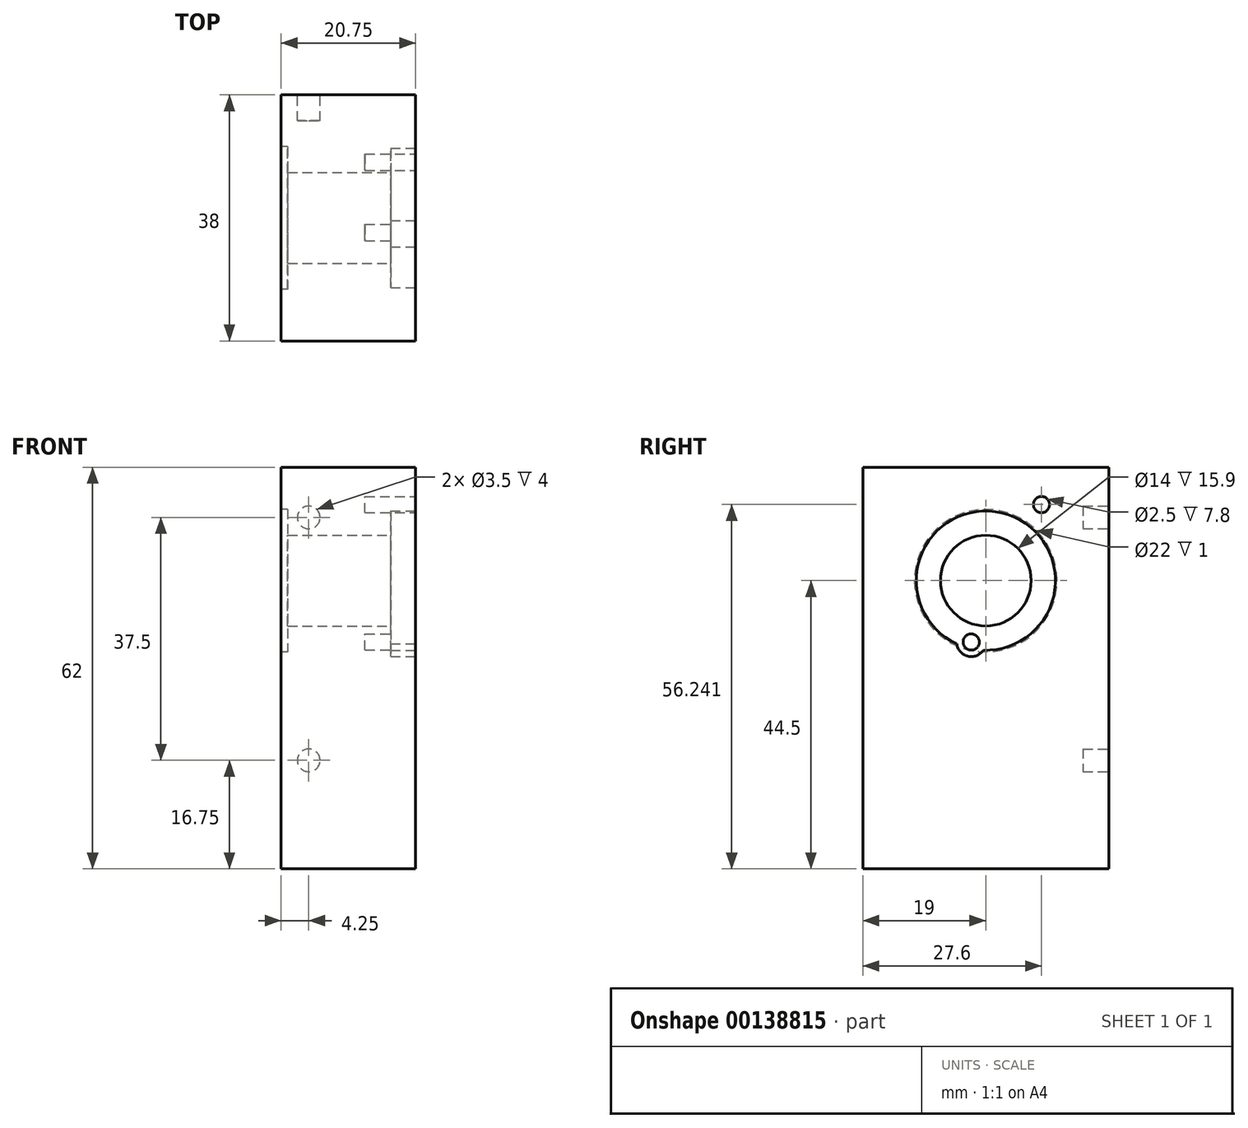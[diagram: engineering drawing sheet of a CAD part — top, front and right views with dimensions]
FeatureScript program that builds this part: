
annotation { "Feature Type Name" : "Feature", "Feature Type Description" : "" }
export const myFeature = defineFeature(function(context is Context, id is Id, definition is map)
    precondition{}
    {
        {
            var Q0;
            Q0=qCreatedBy(makeId("Right.planeOp"),FACE);
            var sketch = newSketch(context, id + "F0", { "sketchPlane" : qUnion([Q0])});
            skLineSegment(sketch, "E0.bottom", {"start": v(-19, -31) * mm, "end": v(19, -31) * mm});
            skLineSegment(sketch, "E0.top", {"start": v(-19, 31) * mm, "end": v(19, 31) * mm});
            skLineSegment(sketch, "E0.left", {"start": v(-19, -31) * mm, "end": v(-19, 31) * mm});
            skLineSegment(sketch, "E0.right", {"start": v(19, -31) * mm, "end": v(19, 31) * mm});
            skPoint(sketch, "E0.middle", {"position": v(0, 0) * mm});
            skSolve(sketch);
        }
        {
            var Q0;
            Q0 = qSketchRegion(id + "F0", true);
            extrude(context, id + "F1", {"entities" : qUnion([Q0]), "depth" : 20.75 * mm});
        }
        {
            var Q0;
            Q0=makeQuery(id+"F1.opExtrude","CAP_FACE",FACE,{"disambiguationData":[OSD([sQuery(id+"F0.wireOp",EDGE,"E0.bottom"),sQuery(id+"F0.wireOp",EDGE,"E0.top"),sQuery(id+"F0.wireOp",EDGE,"E0.left"),sQuery(id+"F0.wireOp",EDGE,"E0.right")])],"isStart":false});
            var sketch = newSketch(context, id + "F2", { "sketchPlane" : qUnion([Q0])});
            skLineSegment(sketch, "E1", {"start": v(0, 31) * mm, "end": v(0, -31) * mm, "construction": true});
            skCircle(sketch, "E2", {"center": v(0, 13.5) * mm, "radius": 7 * mm});
            skArc(sketch, "E3", {"start": v(-0.38, 2.76) * mm, "mid": v(2.48, 23.96) * mm, "end": v(-4.48, 3.73) * mm});
            skLineSegment(sketch, "E4", {"start": v(0, 24) * mm, "end": v(8.6, 24) * mm, "construction": true});
            skCircle(sketch, "E5", {"center": v(8.6, 25.24) * mm, "radius": 1.25 * mm});
            skCircle(sketch, "E6", {"center": v(-2.25, 4.01) * mm, "radius": 1.25 * mm});
            skArc(sketch, "E7.0", {"start": v(-4.48, 3.73) * mm, "mid": v(-2.77, 1.82) * mm, "end": v(-0.38, 2.76) * mm});
            skSolve(sketch);
        }
        {
            var Q0;
            Q0=makeQuery(id+"F2.imprint","IMPRINT",FACE,{"disambiguationData":[TD([[makeQuery(id+"F2.imprint","IMPRINT",EDGE,{"derivedFrom":sQuery(id+"F2.wireOp",EDGE,"E2")}),-1.0]])]});
            extrude(context, id + "F3", {"entities" : qUnion([Q0]), "operationType" : NewBodyOperationType.REMOVE, "oppositeDirection" : true, "depth" : 3.85 * mm});
        }
        {
            var Q0;
            Q0=makeQuery(id+"F2.imprint","IMPRINT",FACE,{"disambiguationData":[TD([[makeQuery(id+"F2.imprint","IMPRINT",EDGE,{"derivedFrom":sQuery(id+"F2.wireOp",EDGE,"E6")}),1.0]])]});
            var Q1;
            Q1=makeQuery(id+"F2.imprint","IMPRINT",FACE,{"disambiguationData":[TD([[makeQuery(id+"F2.imprint","IMPRINT",EDGE,{"derivedFrom":sQuery(id+"F2.wireOp",EDGE,"E5")}),1.0]])]});
            extrude(context, id + "F4", {"entities" : qUnion([Q0, Q1]), "operationType" : NewBodyOperationType.REMOVE, "oppositeDirection" : true, "depth" : 7.8 * mm});
        }
        {
            var Q0;
            Q0=makeQuery(id+"F2.imprint","IMPRINT",FACE,{"disambiguationData":[TD([[makeQuery(id+"F2.imprint","IMPRINT",EDGE,{"derivedFrom":sQuery(id+"F2.wireOp",EDGE,"E2")}),1.0]])]});
            extrude(context, id + "F5", {"entities" : qUnion([Q0]), "operationType" : NewBodyOperationType.REMOVE, "endBound" : BoundingType.THROUGH_ALL, "oppositeDirection" : true, "depth" : 25 * mm});
        }
        {
            var Q0;
            Q0=makeQuery(id+"F1.opExtrude","CAP_FACE",FACE,{"disambiguationData":[OSD([sQuery(id+"F0.wireOp",EDGE,"E0.bottom"),sQuery(id+"F0.wireOp",EDGE,"E0.top"),sQuery(id+"F0.wireOp",EDGE,"E0.left"),sQuery(id+"F0.wireOp",EDGE,"E0.right")])],"isStart":true});
            var sketch = newSketch(context, id + "F6", { "sketchPlane" : qUnion([Q0])});
            skCircle(sketch, "E8", {"center": v(0, 13.5) * mm, "radius": 11 * mm});
            skSolve(sketch);
        }
        {
            var Q0;
            Q0=makeQuery(id+"F6.imprint","IMPRINT",FACE,{"disambiguationData":[TD([[makeQuery(id+"F6.imprint","IMPRINT",EDGE,{"derivedFrom":sQuery(id+"F6.wireOp",EDGE,"E8")}),1.0]])]});
            extrude(context, id + "F7", {"entities" : qUnion([Q0]), "operationType" : NewBodyOperationType.REMOVE, "oppositeDirection" : true, "depth" : 1 * mm});
        }
        {
            var Q0;
            Q0=makeQuery(id+"F1.opExtrude","SWEPT_FACE",FACE,{"disambiguationData":[OSD([sQuery(id+"F0.wireOp",EDGE,"E0.right")])]});
            var sketch = newSketch(context, id + "F8", { "sketchPlane" : qUnion([Q0])});
            skCircle(sketch, "E9", {"center": v(-4.25, 23.25) * mm, "radius": 1.75 * mm});
            skCircle(sketch, "E10", {"center": v(-4.25, -14.25) * mm, "radius": 1.75 * mm});
            skSolve(sketch);
        }
        {
            var Q0;
            Q0 = qSketchRegion(id + "F8", true);
            extrude(context, id + "F9", {"entities" : qUnion([Q0]), "operationType" : NewBodyOperationType.REMOVE, "oppositeDirection" : true, "depth" : 4 * mm});
        }
    });
